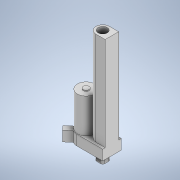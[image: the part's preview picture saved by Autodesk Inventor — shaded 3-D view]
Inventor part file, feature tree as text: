
AUTODESK INVENTOR PART (.ipt)
format: ipt  version: 2022 (Build 260153000, 153)  size: 196,096 bytes
history: native  units: mm
features: extrude x8, sketch x8, fillet x1, chamfer x1
ambient origin geometry x8: Origin, YZ Plane, XZ Plane, XY Plane, X Axis, Y Axis, Z Axis, Center Point
bodies: Solid1 (feature_tree)
feature tree (18):
  extrude  "Extrusion1"  Depth=29.5mm
  extrude  "Extrusion2"  Depth=40.55mm
  extrude  "Extrusion3"  Depth=38.5mm
  extrude  "Extrusion4"  Depth=22.3mm
  extrude  "Extrusion5"  Depth=150.0mm
  extrude  "Extrusion6"  Depth=2.0mm
  fillet  "Fillet1"  Radius=2.0mm
  extrude  "Extrusion7"  Depth=17.8mm
  chamfer  "Chamfer1"  Distance=40.0mm Angle=360.0deg
  extrude  "Extrusion8"  Depth=18.8mm TaperAngle=0.0deg
  sketch  "Sketch1"  dims[d0=29.5mm d1=35.0mm]
  sketch  "Sketch2"  dims[d2=204.3mm d3=0.0mm d4=40.55mm]
  sketch  "Sketch3"  dims[d5=75.55mm d6=38.5mm]
  sketch  "Sketch4"  dims[d7=22.3mm d8=0.0mm d9=20.1mm]
  sketch  "Sketch5"  dims[d10=150.0mm d11=0.0mm d12=38.1mm]
  sketch  "Sketch6"  dims[d13=75.3mm d14=0.0mm d15=12.75mm d16=2.0mm d17=0.0mm]
  sketch  "Sketch7"  dims[d18=17.8mm d19=17.8mm d20=40.0mm d22=360.0deg]
  sketch  "Sketch8"  dims[d24=8.5mm d25=18.8mm d26=0.0mm d27=2.0mm d28=6.9mm d29=6.35mm d30=0.0mm d31=0.0mm d32=1.0mm d33=2.0mm d34=45.0deg d35=28.0mm d36=17.0mm d37=12.1mm d38=10.0mm d39=0.0mm]
